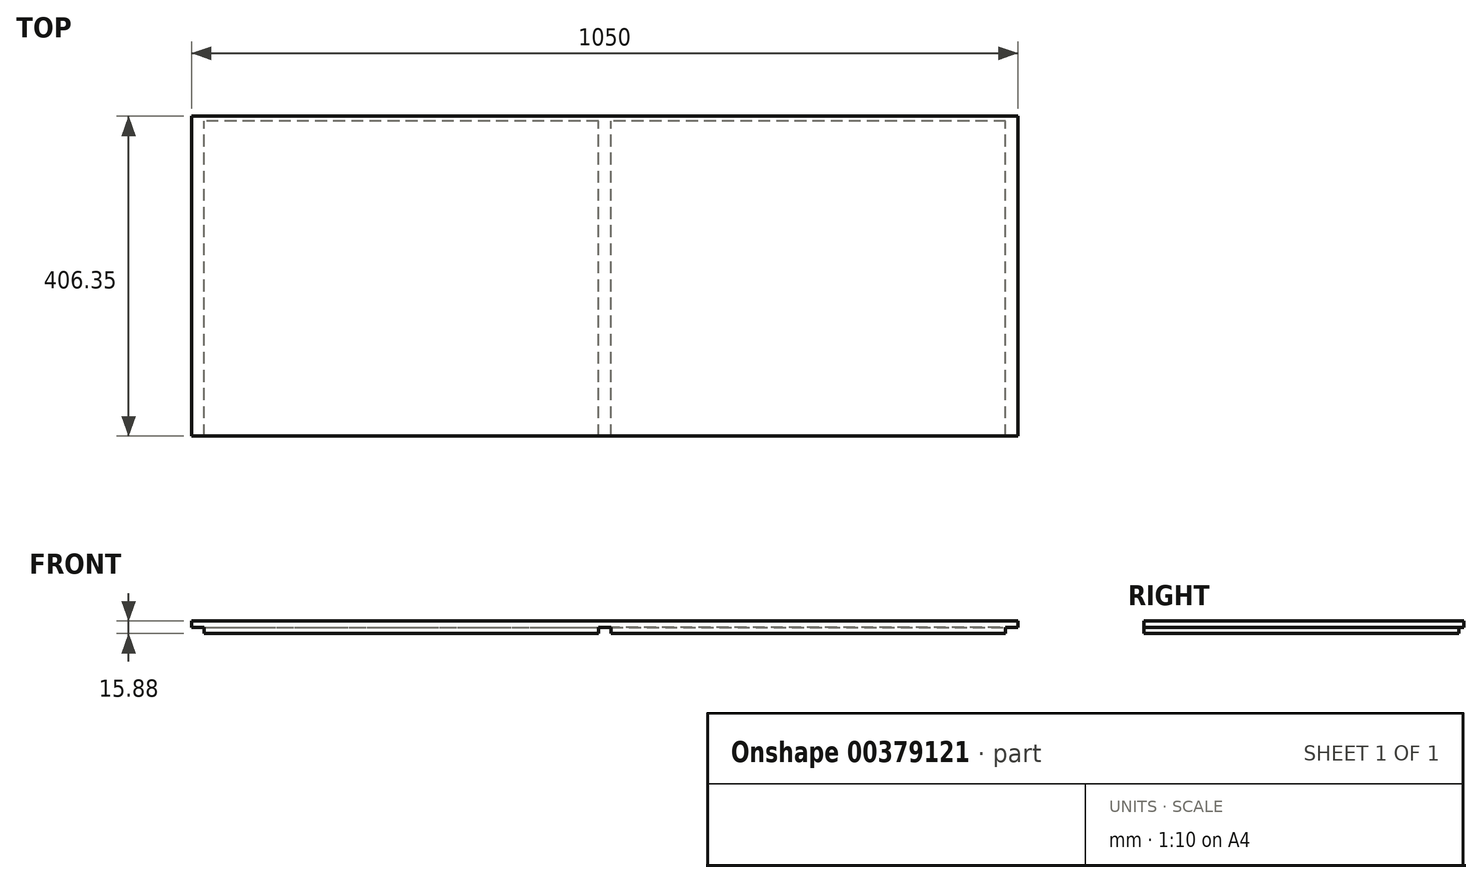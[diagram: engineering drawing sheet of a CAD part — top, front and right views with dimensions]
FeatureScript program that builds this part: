
annotation { "Feature Type Name" : "Feature", "Feature Type Description" : "" }
export const myFeature = defineFeature(function(context is Context, id is Id, definition is map)
    precondition{}
    {
        {
            var Q0;
            Q0=qCreatedBy(makeId("Front.planeOp"),FACE);
            var sketch = newSketch(context, id + "F0", { "sketchPlane" : qUnion([Q0])});
            skLineSegment(sketch, "E0.bottom", {"start": v(525, 7.94) * mm, "end": v(-525, 7.94) * mm});
            skLineSegment(sketch, "E0.top", {"start": v(525, -7.94) * mm, "end": v(-525, -7.94) * mm});
            skLineSegment(sketch, "E0.left", {"start": v(525, 7.94) * mm, "end": v(525, -7.94) * mm});
            skLineSegment(sketch, "E0.right", {"start": v(-525, 7.94) * mm, "end": v(-525, -7.94) * mm});
            skPoint(sketch, "E0.middle", {"position": v(0, 0) * mm});
            skLineSegment(sketch, "E1.bottom", {"start": v(-525, -7.94) * mm, "end": v(-509.12, -7.94) * mm});
            skLineSegment(sketch, "E1.top", {"start": v(-525, 0) * mm, "end": v(-509.12, 0) * mm});
            skLineSegment(sketch, "E1.left", {"start": v(-525, -7.94) * mm, "end": v(-525, 0) * mm});
            skLineSegment(sketch, "E1.right", {"start": v(-509.12, -7.94) * mm, "end": v(-509.12, 0) * mm});
            skLineSegment(sketch, "E2.bottom", {"start": v(525, -7.94) * mm, "end": v(509.12, -7.94) * mm});
            skLineSegment(sketch, "E2.top", {"start": v(525, 0) * mm, "end": v(509.12, 0) * mm});
            skLineSegment(sketch, "E2.left", {"start": v(525, -7.94) * mm, "end": v(525, 0) * mm});
            skLineSegment(sketch, "E2.right", {"start": v(509.12, -7.94) * mm, "end": v(509.12, 0) * mm});
            skLineSegment(sketch, "E3.bottom", {"start": v(7.94, -7.94) * mm, "end": v(-7.94, -7.94) * mm});
            skLineSegment(sketch, "E3.top", {"start": v(7.94, 0) * mm, "end": v(-7.94, 0) * mm});
            skLineSegment(sketch, "E3.left", {"start": v(7.94, -7.94) * mm, "end": v(7.94, 0) * mm});
            skLineSegment(sketch, "E3.right", {"start": v(-7.94, -7.94) * mm, "end": v(-7.94, 0) * mm});
            skPoint(sketch, "E3.middle", {"position": v(0, -3.97) * mm});
            skSolve(sketch);
        }
        {
            var Q0;
            Q0=makeQuery(id+"F0.imprint","IMPRINT",FACE,{"disambiguationData":[TD([[makeQuery(id+"F0.imprint","IMPRINT",EDGE,{"derivedFrom":sQuery(id+"F0.wireOp",EDGE,"E0.bottom")}),1.0]])]});
            extrude(context, id + "F1", {"entities" : qUnion([Q0]), "depth" : 406.35 * mm});
        }
        {
            var Q0;
            Q0=qCreatedBy(makeId("Right.planeOp"),FACE);
            var sketch = newSketch(context, id + "F2", { "sketchPlane" : qUnion([Q0])});
            skLineSegment(sketch, "E4.bottom", {"start": v(0, 0) * mm, "end": v(-6.35, 0) * mm});
            skLineSegment(sketch, "E4.top", {"start": v(0, -7.95) * mm, "end": v(-6.35, -7.95) * mm});
            skLineSegment(sketch, "E4.left", {"start": v(0, 0) * mm, "end": v(0, -7.95) * mm});
            skLineSegment(sketch, "E4.right", {"start": v(-6.35, 0) * mm, "end": v(-6.35, -7.95) * mm});
            skSolve(sketch);
        }
        {
            var Q0;
            Q0=makeQuery(id+"F2.imprint","IMPRINT",FACE,{"disambiguationData":[TD([[makeQuery(id+"F2.imprint","IMPRINT",EDGE,{"derivedFrom":sQuery(id+"F2.wireOp",EDGE,"E4.bottom")}),1.0]])]});
            extrude(context, id + "F3", {"entities" : qUnion([Q0]), "operationType" : NewBodyOperationType.REMOVE, "endBound" : BoundingType.SYMMETRIC, "oppositeDirection" : true, "depth" : 1050 * mm});
        }
    });
